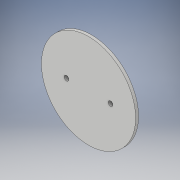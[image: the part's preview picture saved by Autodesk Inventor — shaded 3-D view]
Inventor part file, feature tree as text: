
AUTODESK INVENTOR PART (.ipt)
format: ipt  version: 2019 (Build 230136000, 136)  size: 107,520 bytes
history: native  units: mm
features: sketch x2, other x1, extrude x1, hole x1
ambient origin geometry x8: Origin, YZ Plane, XZ Plane, XY Plane, X Axis, Y Axis, Z Axis, Center Point
bodies: Body1 (feature_tree)
feature tree (5):
  other  "ソリッド1"
  extrude  "押し出し1"  Depth=64.0mm
  hole  "穴1"  [1 undecoded]
  sketch  "スケッチ1"
  sketch  "スケッチ2"
note: 1 required parameter value undecoded (feature->parameter linkage not recoverable at this tier; creation-order binding heuristic only, values carry confidence <= 0.55)
